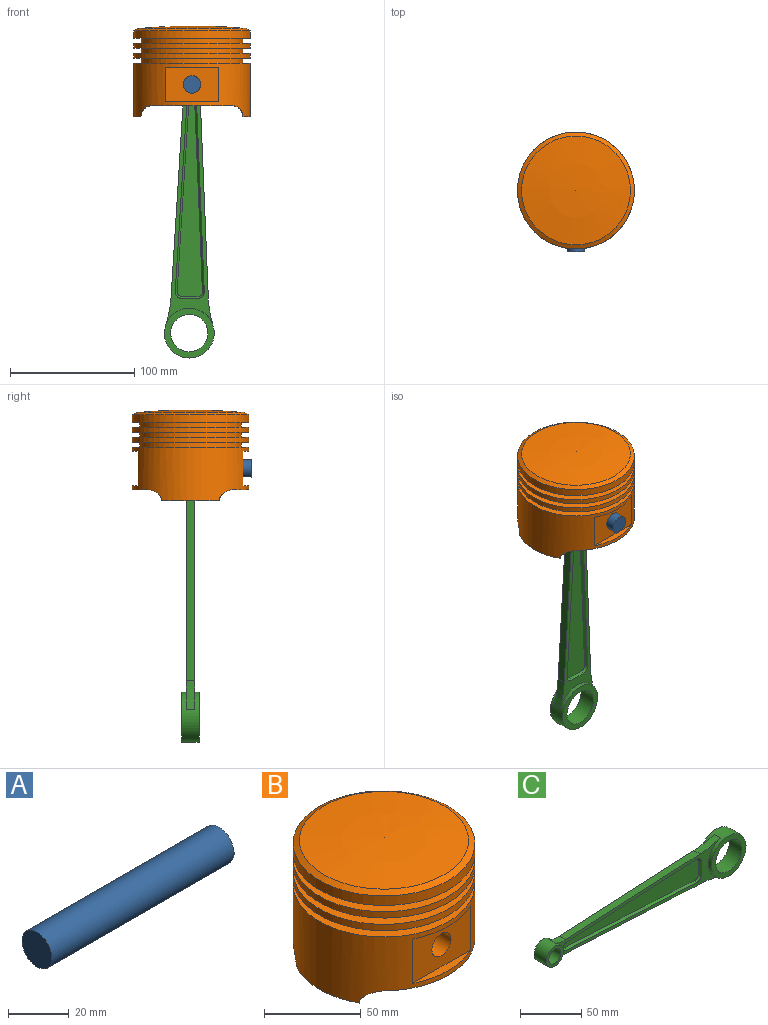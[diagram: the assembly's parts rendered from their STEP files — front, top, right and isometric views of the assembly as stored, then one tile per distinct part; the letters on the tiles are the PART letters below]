
ASSEMBLY  parts=3 mates=2
PART A: 3 faces, bbox 85x14x14 mm
  f0: cylinder r=7mm len=85mm, axis (-1,0,0), area 3738.5mm2, adj f1,f2
  f1: plane 14x14mm, normal (1,0,0), area 153.9mm2, adj f0
  f2: plane 14x14mm, normal (-1,0,0), area 153.9mm2, adj f0
PART B: 43 faces, bbox 94x94x73 mm
  f0: cylinder r=47mm len=94mm, axis (0,0,1), area 8592.9mm2, adj f1,f6,f20,f21,f22,f23,f24,f26
  f1: plane 45.96x6mm, normal (0,0,-1), area 151.6mm2, adj f0,f31,f38,f41
  f2: cylinder r=43mm len=46.65mm, axis (0,0,1), area 270.4mm2, adj f3,f20,f39,f40
  f3: cone r=25mm half-angle=68.7deg, axis (0,0,-1), area 3671.9mm2, adj f2,f31,f32,f37,f38,f39,f40,f41
  f4: cylinder r=7mm len=18mm, axis (0,1,0), area 769.6mm2, adj f25,f32
  f5: cylinder r=7mm len=18mm, axis (0,1,0), area 769.6mm2, adj f30,f32
  f6: plane 94x94mm, normal (0,0,1), area 1658.8mm2, adj f0,f7
  f7: cylinder r=41mm len=82mm, axis (0,0,1), area 1030.4mm2, adj f6,f8
  f8: plane 94x94mm, normal (0,0,-1), area 1658.8mm2, adj f7,f9
  f9: cylinder r=47mm len=94mm, axis (0,0,1), area 1181.2mm2, adj f8,f10
  f10: plane 94x94mm, normal (0,0,1), area 1658.8mm2, adj f9,f11
  f11: cylinder r=41mm len=82mm, axis (0,0,1), area 1030.4mm2, adj f10,f12
  f12: plane 94x94mm, normal (0,0,-1), area 1658.8mm2, adj f11,f13
  f13: cylinder r=47mm len=94mm, axis (0,0,1), area 1181.2mm2, adj f12,f14
  f14: plane 94x94mm, normal (0,0,1), area 1658.8mm2, adj f13,f15
  f15: cylinder r=41mm len=82mm, axis (0,0,1), area 1030.4mm2, adj f14,f16
  f16: plane 94x94mm, normal (0,0,-1), area 1658.8mm2, adj f15,f17
  f17: cylinder r=47mm len=94mm, axis (0,0,1), area 1771.9mm2, adj f16,f18
  f18: cone r=43.74mm half-angle=58.4deg, axis (0,0,-1), area 1089.5mm2, adj f17,f19
  f19: sphere r=479.37mm, area 6023.9mm2, adj f18
  f20: plane 45.96x6mm, normal (0,0,-1), area 151.6mm2, adj f0,f2,f39,f40
  f21: plane 42x5mm, normal (0,0,1), area 142.2mm2, adj f0,f22,f24,f25
  f22: plane 28x0.05mm, normal (-1,0,0), area 1.3mm2, adj f0,f21,f23,f25
  f23: plane 42x5mm, normal (0,0,-1), area 142.2mm2, adj f0,f22,f24,f25
  f24: plane 28x0.05mm, normal (1,0,0), area 1.3mm2, adj f0,f21,f23,f25
  f25: plane 42x28mm, normal (0,-1,0), area 1022.1mm2, adj f4,f21,f22,f23,f24
  f26: plane 42x5mm, normal (0,0,1), area 142.2mm2, adj f0,f27,f29,f30
  f27: plane 28x0.05mm, normal (1,0,0), area 1.3mm2, adj f0,f26,f28,f30
  f28: plane 42x5mm, normal (0,0,-1), area 142.2mm2, adj f0,f27,f29,f30
  f29: plane 28x0.05mm, normal (-1,0,0), area 1.3mm2, adj f0,f26,f28,f30
  f30: plane 42x28mm, normal (0,1,0), area 1022.1mm2, adj f5,f26,f27,f28,f29
  f31: cylinder r=43mm len=46.65mm, axis (0,0,1), area 270.3mm2, adj f1,f3,f38,f41
  f32: cylinder r=25mm len=50mm, axis (0,0,1), area 3459mm2, adj f3,f4,f5,f33
  f33: plane 56x56mm, normal (0,0,1), area 499.5mm2, adj f32,f34
  f34: torus R=28mm, axis (0,0,1), area 2612.9mm2, adj f33,f35
  f35: cylinder r=36mm len=72mm, axis (0,0,1), area 3619.1mm2, adj f34,f36
  f36: plane 72x72mm, normal (0,0,-1), area 4071.5mm2, adj f35
  f37: plane 64x22.29mm, normal (0,0,-1), area 472.5mm2, adj f0,f3,f38,f39
  f38: cylinder r=9mm len=21.46mm, axis (0,1,0), area 123.1mm2, adj f0,f1,f3,f31,f37
  f39: cylinder r=9mm len=21.46mm, axis (0,1,0), area 123.1mm2, adj f0,f2,f3,f20,f37
  f40: cylinder r=9mm len=21.46mm, axis (0,1,0), area 123.1mm2, adj f0,f2,f3,f20,f42
  f41: cylinder r=9mm len=21.46mm, axis (0,1,0), area 123.1mm2, adj f0,f1,f3,f31,f42
  f42: plane 64x22.29mm, normal (0,0,-1), area 472.5mm2, adj f0,f3,f40,f41
PART C: 30 faces, bbox 230x14x40 mm
  f0: cylinder r=26mm len=11.78mm, axis (0,1,0), area 84.6mm2, adj f5,f6,f7,f9
  f1: cylinder r=26mm len=11.78mm, axis (0,1,0), area 84.6mm2, adj f2,f6,f7,f9
  f2: plane 154.8x7.93mm, normal (-0.05,0,-1), area 1085mm2, adj f1,f3,f6,f7
  f3: cylinder r=96mm len=23.49mm, axis (0,1,0), area 167.4mm2, adj f2,f6,f7,f13
  f4: cylinder r=96mm len=23.49mm, axis (0,1,0), area 167.4mm2, adj f5,f6,f7,f13
  f5: plane 154.8x7.93mm, normal (-0.05,0,1), area 1085mm2, adj f0,f4,f6,f7
  f6: plane 190.06x38.21mm, normal (0,-1,0), area 1390.1mm2, adj f0,f1,f2,f3,f4,f5,f9,f13
  f7: plane 190.06x38.21mm, normal (0,1,0), area 1390.1mm2, adj f0,f1,f2,f3,f4,f5,f9,f13
  f8: cylinder r=7mm len=14mm, axis (0,1,0), area 615.8mm2, adj f10,f11
  f9: cylinder r=10mm len=20mm, axis (0,1,0), area 717.6mm2, adj f0,f1,f6,f7,f10,f11
  f10: plane 20x20mm, normal (0,-1,0), area 160.2mm2, adj f8,f9
  f11: plane 20x20mm, normal (0,1,0), area 160.2mm2, adj f8,f9
  f12: cylinder r=15mm len=30mm, axis (0,1,0), area 1319.5mm2, adj f14,f15
  f13: cylinder r=20mm len=40mm, axis (0,1,0), area 1403.6mm2, adj f3,f4,f6,f7,f14,f15
  f14: plane 40x40mm, normal (0,-1,0), area 549.8mm2, adj f12,f13
  f15: plane 40x40mm, normal (0,1,0), area 549.8mm2, adj f12,f13
  f16: plane 156x20.37mm, normal (0,-1,0), area 1979.8mm2, adj f17,f18,f19,f20,f21,f22
  f17: cone r=2.5mm half-angle=36.9deg, axis (0,-1,0), area 24.7mm2, adj f6,f16,f18,f22
  f18: plane 150.03x9.18mm, normal (0.04,-0.6,0.8), area 375.4mm2, adj f6,f16,f17,f19
  f19: cone r=3.5mm half-angle=36.9deg, axis (0,-1,0), area 17.2mm2, adj f6,f16,f18,f20
  f20: plane 13.37x2mm, normal (-0.8,-0.6,0), area 33.4mm2, adj f6,f16,f19,f21
  f21: cone r=3.5mm half-angle=36.9deg, axis (0,-1,0), area 17.2mm2, adj f6,f16,f20,f22
  f22: plane 150.03x9.18mm, normal (0.04,-0.6,-0.8), area 375.4mm2, adj f6,f16,f17,f21
  f23: plane 156x20.37mm, normal (0,1,0), area 1979.8mm2, adj f24,f25,f26,f27,f28,f29
  f24: cone r=2.5mm half-angle=36.9deg, axis (0,1,0), area 24.7mm2, adj f7,f23,f25,f29
  f25: plane 150.03x9.18mm, normal (0.04,0.6,0.8), area 375.4mm2, adj f7,f23,f24,f26
  f26: cone r=3.5mm half-angle=36.9deg, axis (0,1,0), area 17.2mm2, adj f7,f23,f25,f27
  f27: plane 13.37x2mm, normal (-0.8,0.6,0), area 33.4mm2, adj f7,f23,f26,f28
  f28: cone r=3.5mm half-angle=36.9deg, axis (0,1,0), area 17.2mm2, adj f7,f23,f27,f29
  f29: plane 150.03x9.18mm, normal (0.04,0.6,-0.8), area 375.4mm2, adj f7,f23,f24,f28
PLACE A rot(axis=(0.58,-0.58,-0.58),120deg) t=(-131.13,-30.98,3.14)mm
PLACE B t=(-131.13,-66.62,-40.86)mm fixed
PLACE C rot(axis=(0,1,0),90.6deg) t=(-131.13,-66.48,3.14)mm
MATE slider A.f0 <-> B.f4  axis (0,1,0) through (-131.13,-73.48,3.14)mm
MATE revolute C.f8 <-> A.f0  axis (0,-1,0) through (-131.13,-73.48,3.14)mm
